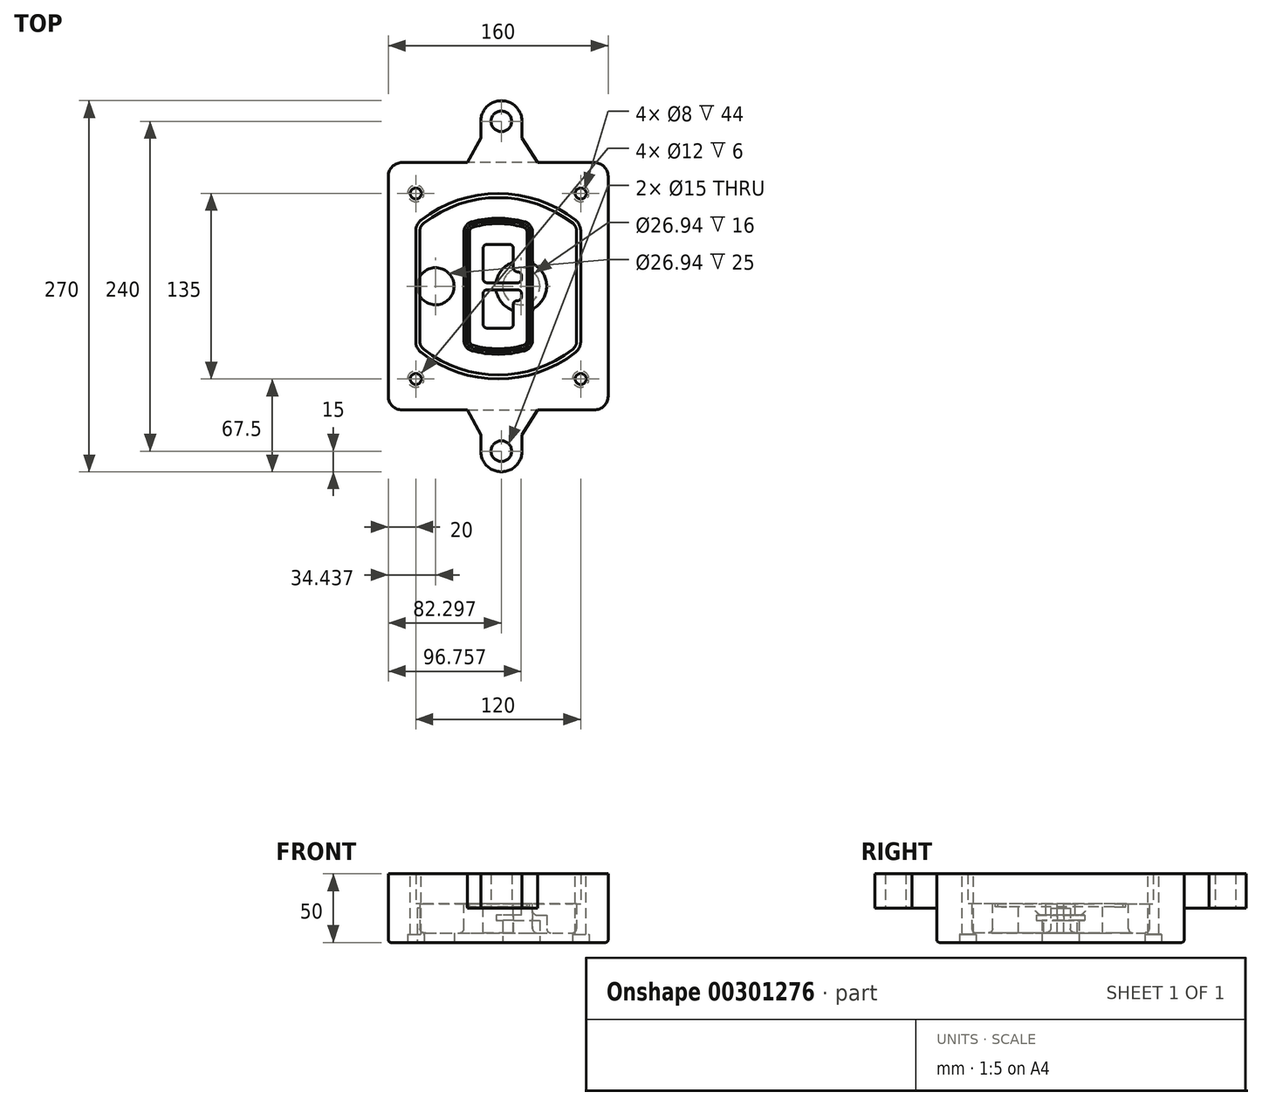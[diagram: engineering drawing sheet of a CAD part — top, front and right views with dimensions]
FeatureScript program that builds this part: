
annotation { "Feature Type Name" : "Feature", "Feature Type Description" : "" }
export const myFeature = defineFeature(function(context is Context, id is Id, definition is map)
    precondition{}
    {
        {
            var Q0;
            Q0=qCreatedBy(makeId("Top.planeOp"),FACE);
            var sketch = newSketch(context, id + "F0", { "sketchPlane" : qUnion([Q0])});
            skPoint(sketch, "E0.rect.middle", {"position": v(0, 0) * mm});
            skLineSegment(sketch, "E1.bottom", {"start": v(-70, -90) * mm, "end": v(70, -90) * mm});
            skLineSegment(sketch, "E1.top", {"start": v(-70, 90) * mm, "end": v(70, 90) * mm});
            skLineSegment(sketch, "E1.left", {"start": v(-80, -80) * mm, "end": v(-80, 80) * mm});
            skLineSegment(sketch, "E1.right", {"start": v(80, -80) * mm, "end": v(80, 80) * mm});
            skLineSegment(sketch, "E2", {"start": v(-80, 90) * mm, "end": v(80, -90) * mm, "construction": true});
            skLineSegment(sketch, "E3", {"start": v(80, 90) * mm, "end": v(-80, -90) * mm, "construction": true});
            skCircle(sketch, "E4", {"center": v(-60, 67.5) * mm, "radius": 4 * mm});
            skCircle(sketch, "E5", {"center": v(60, 67.5) * mm, "radius": 4 * mm});
            skCircle(sketch, "E6", {"center": v(60, -67.5) * mm, "radius": 4 * mm});
            skCircle(sketch, "E7", {"center": v(-60, -67.5) * mm, "radius": 4 * mm});
            skLineSegment(sketch, "E8", {"start": v(-60, 67.5) * mm, "end": v(60, 67.5) * mm, "construction": true});
            skLineSegment(sketch, "E9", {"start": v(60, 67.5) * mm, "end": v(60, -67.5) * mm, "construction": true});
            skLineSegment(sketch, "E10", {"start": v(60, -67.5) * mm, "end": v(-60, -67.5) * mm, "construction": true});
            skLineSegment(sketch, "E11", {"start": v(-60, -67.5) * mm, "end": v(-60, 67.5) * mm, "construction": true});
            skLineSegment(sketch, "E12", {"start": v(-60, 40.3) * mm, "end": v(-60, -40.3) * mm});
            skLineSegment(sketch, "E13", {"start": v(60, 40.3) * mm, "end": v(60, -40.3) * mm});
            skArc(sketch, "E14", {"start": v(56.15, 48.18) * mm, "mid": v(0, 67.5) * mm, "end": v(-56.15, 48.18) * mm});
            skArc(sketch, "E15", {"start": v(-56.15, -48.18) * mm, "mid": v(0, -67.5) * mm, "end": v(56.15, -48.18) * mm});
            skLineSegment(sketch, "E16", {"start": v(-60, 0) * mm, "end": v(60, 0) * mm, "construction": true});
            skPoint(sketch, "E17.visualSharp", {"position": v(-60, -45) * mm});
            skArc(sketch, "E17.filletArc", {"start": v(-60, -40.3) * mm, "mid": v(-58.99, -44.68) * mm, "end": v(-56.15, -48.18) * mm});
            skPoint(sketch, "E18.visualSharp", {"position": v(-60, 45) * mm});
            skArc(sketch, "E18.filletArc", {"start": v(-56.15, 48.18) * mm, "mid": v(-58.99, 44.68) * mm, "end": v(-60, 40.3) * mm});
            skPoint(sketch, "E19.visualSharp", {"position": v(60, 45) * mm});
            skArc(sketch, "E19.filletArc", {"start": v(60, 40.3) * mm, "mid": v(58.99, 44.68) * mm, "end": v(56.15, 48.18) * mm});
            skPoint(sketch, "E20.visualSharp", {"position": v(60, -45) * mm});
            skArc(sketch, "E20.filletArc", {"start": v(56.15, -48.18) * mm, "mid": v(58.99, -44.68) * mm, "end": v(60, -40.3) * mm});
            skPoint(sketch, "E21.visualSharp", {"position": v(-80, 90) * mm});
            skArc(sketch, "E21.filletArc", {"start": v(-70, 90) * mm, "mid": v(-77.07, 87.07) * mm, "end": v(-80, 80) * mm});
            skPoint(sketch, "E22.visualSharp", {"position": v(80, 90) * mm});
            skArc(sketch, "E22.filletArc", {"start": v(80, 80) * mm, "mid": v(77.07, 87.07) * mm, "end": v(70, 90) * mm});
            skPoint(sketch, "E23.visualSharp", {"position": v(80, -90) * mm});
            skArc(sketch, "E23.filletArc", {"start": v(70, -90) * mm, "mid": v(77.07, -87.07) * mm, "end": v(80, -80) * mm});
            skPoint(sketch, "E24.visualSharp", {"position": v(-80, -90) * mm});
            skArc(sketch, "E24.filletArc", {"start": v(-80, -80) * mm, "mid": v(-77.07, -87.07) * mm, "end": v(-70, -90) * mm});
            skArc(sketch, "E25.0", {"start": v(57, 40.3) * mm, "mid": v(56.3, 43.36) * mm, "end": v(54.3, 45.81) * mm});
            skLineSegment(sketch, "E25.1", {"start": v(57, 40.3) * mm, "end": v(57, -40.3) * mm});
            skArc(sketch, "E25.2", {"start": v(54.3, -45.81) * mm, "mid": v(56.3, -43.36) * mm, "end": v(57, -40.3) * mm});
            skArc(sketch, "E25.3", {"start": v(-54.3, -45.81) * mm, "mid": v(0, -64.5) * mm, "end": v(54.3, -45.81) * mm});
            skArc(sketch, "E25.4", {"start": v(-57, -40.3) * mm, "mid": v(-56.3, -43.36) * mm, "end": v(-54.3, -45.81) * mm});
            skArc(sketch, "E25.5", {"start": v(54.3, 45.81) * mm, "mid": v(0, 64.5) * mm, "end": v(-54.3, 45.81) * mm});
            skLineSegment(sketch, "E25.6", {"start": v(-57, 40.3) * mm, "end": v(-57, -40.3) * mm});
            skArc(sketch, "E25.7", {"start": v(-54.3, 45.81) * mm, "mid": v(-56.3, 43.36) * mm, "end": v(-57, 40.3) * mm});
            skArc(sketch, "E26.0", {"start": v(-58.62, 51.33) * mm, "mid": v(-62.58, 46.43) * mm, "end": v(-64, 40.3) * mm});
            skArc(sketch, "E26.1", {"start": v(58.62, 51.33) * mm, "mid": v(0, 71.5) * mm, "end": v(-58.62, 51.33) * mm});
            skArc(sketch, "E26.2", {"start": v(64, 40.3) * mm, "mid": v(62.58, 46.43) * mm, "end": v(58.62, 51.33) * mm});
            skLineSegment(sketch, "E26.3", {"start": v(64, 40.3) * mm, "end": v(64, -40.3) * mm});
            skArc(sketch, "E26.4", {"start": v(58.62, -51.33) * mm, "mid": v(62.58, -46.43) * mm, "end": v(64, -40.3) * mm});
            skLineSegment(sketch, "E26.5", {"start": v(-64, 40.3) * mm, "end": v(-64, -40.3) * mm});
            skArc(sketch, "E26.6", {"start": v(-58.62, -51.33) * mm, "mid": v(0, -71.5) * mm, "end": v(58.62, -51.33) * mm});
            skArc(sketch, "E26.7", {"start": v(-64, -40.3) * mm, "mid": v(-62.58, -46.43) * mm, "end": v(-58.62, -51.33) * mm});
            skSolve(sketch);
        }
        {
            var Q0;
            Q0=makeQuery(id+"F0.imprint","IMPRINT",FACE,{"disambiguationData":[TD([[makeQuery(id+"F0.imprint","IMPRINT",EDGE,{"derivedFrom":sQuery(id+"F0.wireOp",EDGE,"E1.bottom")}),1.0]])]});
            var Q1;
            Q1=makeQuery(id+"F0.imprint","IMPRINT",FACE,{"disambiguationData":[TD([[makeQuery(id+"F0.imprint","IMPRINT",EDGE,{"derivedFrom":sQuery(id+"F0.wireOp",EDGE,"E12")}),1.0]])]});
            var Q2;
            Q2=makeQuery(id+"F0.imprint","IMPRINT",FACE,{"disambiguationData":[TD([[makeQuery(id+"F0.imprint","IMPRINT",EDGE,{"derivedFrom":sQuery(id+"F0.wireOp",EDGE,"E25.0")}),1.0]])]});
            var Q3;
            Q3=makeQuery(id+"F0.imprint","IMPRINT",FACE,{"disambiguationData":[TD([[makeQuery(id+"F0.imprint","IMPRINT",EDGE,{"derivedFrom":sQuery(id+"F0.wireOp",EDGE,"E12")}),-1.0]])]});
            extrude(context, id + "F1", {"entities" : qUnion([Q0, Q1, Q2, Q3]), "oppositeDirection" : true, "depth" : 25 * mm});
        }
        {
            var Q0;
            Q0=makeQuery(id+"F0.imprint","IMPRINT",FACE,{"disambiguationData":[TD([[makeQuery(id+"F0.imprint","IMPRINT",EDGE,{"derivedFrom":sQuery(id+"F0.wireOp",EDGE,"E12")}),1.0]])]});
            extrude(context, id + "F2", {"entities" : qUnion([Q0]), "operationType" : NewBodyOperationType.ADD, "depth" : 3 * mm});
        }
        {
            var Q0;
            Q0=makeQuery(id+"F0.imprint","IMPRINT",FACE,{"disambiguationData":[TD([[makeQuery(id+"F0.imprint","IMPRINT",EDGE,{"derivedFrom":sQuery(id+"F0.wireOp",EDGE,"E25.0")}),1.0]])]});
            extrude(context, id + "F3", {"entities" : qUnion([Q0]), "operationType" : NewBodyOperationType.REMOVE, "oppositeDirection" : true, "depth" : 18 * mm});
        }
        {
            var Q0;
            Q0=makeQuery(id+"F2.opExtrude","CAP_FACE",FACE,{"disambiguationData":[OSD([sQuery(id+"F0.wireOp",EDGE,"E12"),sQuery(id+"F0.wireOp",EDGE,"E13"),sQuery(id+"F0.wireOp",EDGE,"E14"),sQuery(id+"F0.wireOp",EDGE,"E15"),sQuery(id+"F0.wireOp",EDGE,"E17.filletArc"),sQuery(id+"F0.wireOp",EDGE,"E18.filletArc"),sQuery(id+"F0.wireOp",EDGE,"E19.filletArc"),sQuery(id+"F0.wireOp",EDGE,"E20.filletArc"),sQuery(id+"F0.wireOp",EDGE,"E25.0"),sQuery(id+"F0.wireOp",EDGE,"E25.1"),sQuery(id+"F0.wireOp",EDGE,"E25.2"),sQuery(id+"F0.wireOp",EDGE,"E25.3"),sQuery(id+"F0.wireOp",EDGE,"E25.4"),sQuery(id+"F0.wireOp",EDGE,"E25.5"),sQuery(id+"F0.wireOp",EDGE,"E25.6"),sQuery(id+"F0.wireOp",EDGE,"E25.7")])],"isStart":false});
            var sketch = newSketch(context, id + "F4", { "sketchPlane" : qUnion([Q0])});
            skArc(sketch, "E27.0", {"start": v(-19.08, -46.97) * mm, "mid": v(0, -49.5) * mm, "end": v(19.08, -46.97) * mm});
            skArc(sketch, "E28.0", {"start": v(19.08, 46.97) * mm, "mid": v(0, 49.5) * mm, "end": v(-19.08, 46.97) * mm});
            skLineSegment(sketch, "E29", {"start": v(-25, 39.25) * mm, "end": v(-25, -39.25) * mm});
            skLineSegment(sketch, "E30", {"start": v(25, 39.25) * mm, "end": v(25, -39.25) * mm});
            skLineSegment(sketch, "E31", {"start": v(-25, 45.1) * mm, "end": v(25, 45.1) * mm, "construction": true});
            skLineSegment(sketch, "E32", {"start": v(-25, -45.1) * mm, "end": v(25, -45.1) * mm, "construction": true});
            skPoint(sketch, "E33.visualSharp", {"position": v(-25, 45.1) * mm});
            skArc(sketch, "E33.filletArc", {"start": v(-19.08, 46.97) * mm, "mid": v(-23.35, 44.11) * mm, "end": v(-25, 39.25) * mm});
            skPoint(sketch, "E34.visualSharp", {"position": v(25, 45.1) * mm});
            skArc(sketch, "E34.filletArc", {"start": v(25, 39.25) * mm, "mid": v(23.35, 44.11) * mm, "end": v(19.08, 46.97) * mm});
            skPoint(sketch, "E35.visualSharp", {"position": v(25, -45.1) * mm});
            skArc(sketch, "E35.filletArc", {"start": v(19.08, -46.97) * mm, "mid": v(23.35, -44.11) * mm, "end": v(25, -39.25) * mm});
            skPoint(sketch, "E36.visualSharp", {"position": v(-25, -45.1) * mm});
            skArc(sketch, "E36.filletArc", {"start": v(-25, -39.25) * mm, "mid": v(-23.35, -44.11) * mm, "end": v(-19.08, -46.97) * mm});
            skArc(sketch, "E37.0", {"start": v(54.3, 45.81) * mm, "mid": v(0, 64.5) * mm, "end": v(-54.3, 45.81) * mm});
            skArc(sketch, "E37.1", {"start": v(-54.3, 45.81) * mm, "mid": v(-56.3, 43.36) * mm, "end": v(-57, 40.3) * mm});
            skLineSegment(sketch, "E37.2", {"start": v(-57, 40.3) * mm, "end": v(-57, -40.3) * mm});
            skArc(sketch, "E37.3", {"start": v(-57, -40.3) * mm, "mid": v(-56.3, -43.36) * mm, "end": v(-54.3, -45.81) * mm});
            skArc(sketch, "E37.4", {"start": v(-54.3, -45.81) * mm, "mid": v(0, -64.5) * mm, "end": v(54.3, -45.81) * mm});
            skArc(sketch, "E37.5", {"start": v(54.3, -45.81) * mm, "mid": v(56.3, -43.36) * mm, "end": v(57, -40.3) * mm});
            skLineSegment(sketch, "E37.6", {"start": v(57, 40.3) * mm, "end": v(57, -40.3) * mm});
            skArc(sketch, "E37.7", {"start": v(57, 40.3) * mm, "mid": v(56.3, 43.36) * mm, "end": v(54.3, 45.81) * mm});
            skLineSegment(sketch, "E38.0", {"start": v(23, 39.25) * mm, "end": v(23, -39.25) * mm});
            skArc(sketch, "E38.1", {"start": v(18.56, -45.04) * mm, "mid": v(21.76, -42.9) * mm, "end": v(23, -39.25) * mm});
            skArc(sketch, "E38.2", {"start": v(-18.56, -45.04) * mm, "mid": v(0, -47.5) * mm, "end": v(18.56, -45.04) * mm});
            skArc(sketch, "E38.3", {"start": v(-23, -39.25) * mm, "mid": v(-21.76, -42.9) * mm, "end": v(-18.56, -45.04) * mm});
            skLineSegment(sketch, "E38.4", {"start": v(-23, 39.25) * mm, "end": v(-23, -39.25) * mm});
            skArc(sketch, "E38.5", {"start": v(23, 39.25) * mm, "mid": v(21.76, 42.9) * mm, "end": v(18.56, 45.04) * mm});
            skArc(sketch, "E38.6", {"start": v(-18.56, 45.04) * mm, "mid": v(-21.76, 42.9) * mm, "end": v(-23, 39.25) * mm});
            skArc(sketch, "E38.7", {"start": v(18.56, 45.04) * mm, "mid": v(0, 47.5) * mm, "end": v(-18.56, 45.04) * mm});
            skArc(sketch, "E39.0", {"start": v(21, 39.25) * mm, "mid": v(20.18, 41.68) * mm, "end": v(18.04, 43.1) * mm});
            skLineSegment(sketch, "E39.1", {"start": v(21, 39.25) * mm, "end": v(21, -39.25) * mm});
            skArc(sketch, "E39.2", {"start": v(18.04, -43.1) * mm, "mid": v(20.18, -41.68) * mm, "end": v(21, -39.25) * mm});
            skArc(sketch, "E39.3", {"start": v(-18.04, -43.1) * mm, "mid": v(0, -45.5) * mm, "end": v(18.04, -43.1) * mm});
            skArc(sketch, "E39.4", {"start": v(-21, -39.25) * mm, "mid": v(-20.18, -41.68) * mm, "end": v(-18.04, -43.1) * mm});
            skArc(sketch, "E39.5", {"start": v(18.04, 43.1) * mm, "mid": v(0, 45.5) * mm, "end": v(-18.04, 43.1) * mm});
            skLineSegment(sketch, "E39.6", {"start": v(-21, 39.25) * mm, "end": v(-21, -39.25) * mm});
            skArc(sketch, "E39.7", {"start": v(-18.04, 43.1) * mm, "mid": v(-20.18, 41.68) * mm, "end": v(-21, 39.25) * mm});
            skLineSegment(sketch, "E40", {"start": v(-25, 0) * mm, "end": v(25, 0) * mm, "construction": true});
            skLineSegment(sketch, "E41", {"start": v(-11, 5.5) * mm, "end": v(-11, 27.5) * mm});
            skLineSegment(sketch, "E42", {"start": v(-8, 30.5) * mm, "end": v(8, 30.5) * mm});
            skLineSegment(sketch, "E43", {"start": v(11, 27.5) * mm, "end": v(11, 13.5) * mm});
            skLineSegment(sketch, "E44", {"start": v(14, 10.5) * mm, "end": v(14, 10.5) * mm});
            skLineSegment(sketch, "E45", {"start": v(17, 7.5) * mm, "end": v(17, 5.5) * mm});
            skLineSegment(sketch, "E46", {"start": v(14, 2.5) * mm, "end": v(-8, 2.5) * mm});
            skPoint(sketch, "E47.visualSharp", {"position": v(-11, 30.5) * mm});
            skArc(sketch, "E47.filletArc", {"start": v(-8, 30.5) * mm, "mid": v(-10.12, 29.62) * mm, "end": v(-11, 27.5) * mm});
            skPoint(sketch, "E48.visualSharp", {"position": v(11, 30.5) * mm});
            skArc(sketch, "E48.filletArc", {"start": v(11, 27.5) * mm, "mid": v(10.12, 29.62) * mm, "end": v(8, 30.5) * mm});
            skPoint(sketch, "E49.visualSharp", {"position": v(11, 10.5) * mm});
            skArc(sketch, "E49.filletArc", {"start": v(11, 13.5) * mm, "mid": v(11.88, 11.38) * mm, "end": v(14, 10.5) * mm});
            skPoint(sketch, "E50.visualSharp", {"position": v(17, 10.5) * mm});
            skArc(sketch, "E50.filletArc", {"start": v(17, 7.5) * mm, "mid": v(16.12, 9.62) * mm, "end": v(14, 10.5) * mm});
            skPoint(sketch, "E51.visualSharp", {"position": v(17, 2.5) * mm});
            skArc(sketch, "E51.filletArc", {"start": v(14, 2.5) * mm, "mid": v(16.12, 3.38) * mm, "end": v(17, 5.5) * mm});
            skPoint(sketch, "E52.visualSharp", {"position": v(-11, 2.5) * mm});
            skArc(sketch, "E52.filletArc", {"start": v(-11, 5.5) * mm, "mid": v(-10.12, 3.38) * mm, "end": v(-8, 2.5) * mm});
            skLineSegment(sketch, "E53.0.MirrorCS", {"start": v(14, -2.5) * mm, "end": v(-8, -2.5) * mm});
            skArc(sketch, "E54.0.MirrorCS", {"start": v(-11, -5.5) * mm, "mid": v(-10.12, -3.38) * mm, "end": v(-8, -2.5) * mm});
            skLineSegment(sketch, "E55.0.MirrorCS", {"start": v(-11, -5.5) * mm, "end": v(-11, -27.5) * mm});
            skArc(sketch, "E56.0.MirrorCS", {"start": v(-8, -30.5) * mm, "mid": v(-10.12, -29.62) * mm, "end": v(-11, -27.5) * mm});
            skLineSegment(sketch, "E57.0.MirrorCS", {"start": v(-8, -30.5) * mm, "end": v(8, -30.5) * mm});
            skArc(sketch, "E58.0.MirrorCS", {"start": v(11, -27.5) * mm, "mid": v(10.12, -29.62) * mm, "end": v(8, -30.5) * mm});
            skLineSegment(sketch, "E59.0.MirrorCS", {"start": v(11, -27.5) * mm, "end": v(11, -13.5) * mm});
            skArc(sketch, "E60.0.MirrorCS", {"start": v(11, -13.5) * mm, "mid": v(11.88, -11.38) * mm, "end": v(14, -10.5) * mm});
            skArc(sketch, "E61.0.MirrorCS", {"start": v(17, -7.5) * mm, "mid": v(16.12, -9.62) * mm, "end": v(14, -10.5) * mm});
            skLineSegment(sketch, "E62.0.MirrorCS", {"start": v(17, -7.5) * mm, "end": v(17, -5.5) * mm});
            skArc(sketch, "E63.0.MirrorCS", {"start": v(14, -2.5) * mm, "mid": v(16.12, -3.38) * mm, "end": v(17, -5.5) * mm});
            skSolve(sketch);
        }
        {
            var Q0;
            Q0=makeQuery(id+"F4.imprint","IMPRINT",FACE,{"disambiguationData":[TD([[makeQuery(id+"F4.imprint","IMPRINT",EDGE,{"derivedFrom":sQuery(id+"F4.wireOp",EDGE,"E27.0")}),1.0]])]});
            var Q1;
            Q1=makeQuery(id+"F4.imprint","IMPRINT",FACE,{"disambiguationData":[TD([[makeQuery(id+"F4.imprint","IMPRINT",EDGE,{"derivedFrom":sQuery(id+"F4.wireOp",EDGE,"E38.0")}),-1.0]])]});
            var Q2;
            Q2=makeQuery(id+"F4.imprint","IMPRINT",FACE,{"disambiguationData":[TD([[makeQuery(id+"F4.imprint","IMPRINT",EDGE,{"derivedFrom":sQuery(id+"F4.wireOp",EDGE,"E39.0")}),1.0]])]});
            extrude(context, id + "F5", {"entities" : qUnion([Q0, Q1, Q2]), "operationType" : NewBodyOperationType.ADD, "endBound" : BoundingType.UP_TO_NEXT, "oppositeDirection" : true, "depth" : 25 * mm});
        }
        {
            var Q0;
            Q0=makeQuery(id+"F4.imprint","IMPRINT",FACE,{"disambiguationData":[TD([[makeQuery(id+"F4.imprint","IMPRINT",EDGE,{"derivedFrom":sQuery(id+"F4.wireOp",EDGE,"E38.0")}),-1.0]])]});
            extrude(context, id + "F6", {"entities" : qUnion([Q0]), "operationType" : NewBodyOperationType.REMOVE, "oppositeDirection" : true, "depth" : 2 * mm});
        }
        {
            var Q0;
            Q0=makeQuery(id+"F1.opExtrude","CAP_FACE",FACE,{"disambiguationData":[OSD([sQuery(id+"F0.wireOp",EDGE,"E1.bottom"),sQuery(id+"F0.wireOp",EDGE,"E1.top"),sQuery(id+"F0.wireOp",EDGE,"E1.left"),sQuery(id+"F0.wireOp",EDGE,"E1.right"),sQuery(id+"F0.wireOp",EDGE,"E4"),sQuery(id+"F0.wireOp",EDGE,"E5"),sQuery(id+"F0.wireOp",EDGE,"E6"),sQuery(id+"F0.wireOp",EDGE,"E7"),sQuery(id+"F0.wireOp",EDGE,"E21.filletArc"),sQuery(id+"F0.wireOp",EDGE,"E22.filletArc"),sQuery(id+"F0.wireOp",EDGE,"E23.filletArc"),sQuery(id+"F0.wireOp",EDGE,"E24.filletArc")])],"isStart":false});
            var sketch = newSketch(context, id + "F7", { "sketchPlane" : qUnion([Q0])});
            skCircle(sketch, "E64", {"center": v(16.76, 0) * mm, "radius": 13.47 * mm});
            skCircle(sketch, "E65", {"center": v(-45.56, 0) * mm, "radius": 13.47 * mm});
            skLineSegment(sketch, "E66", {"start": v(80, 0) * mm, "end": v(-80, 0) * mm});
            skCircle(sketch, "E67", {"center": v(16.76, 0) * mm, "radius": 18.47 * mm});
            skCircle(sketch, "E68", {"center": v(60, -67.5) * mm, "radius": 6 * mm});
            skCircle(sketch, "E69", {"center": v(-60, -67.5) * mm, "radius": 6 * mm});
            skCircle(sketch, "E70", {"center": v(-60, 67.5) * mm, "radius": 6 * mm});
            skCircle(sketch, "E71", {"center": v(60, 67.5) * mm, "radius": 6 * mm});
            skSolve(sketch);
        }
        {
            var Q0;
            {var subQ1=sQuery(id+"F7.wireOp",EDGE,"E66");var subQ4=sQuery(id+"F7.wireOp",EDGE,"E64");var subQ6=makeQuery(id+"F7.imprint","INTERSECT",VERTEX,{"disambiguationData":[OD(0.0)],"derivedFrom":[subQ4,subQ1]});Q0=makeQuery(id+"F7.imprint","IMPRINT",FACE,{"disambiguationData":[TD([[makeQuery(id+"F7.imprint","IMPRINT",EDGE,{"disambiguationData":[TD([[subQ6,-1.0]])],"derivedFrom":subQ4}),-1.0]])]});}
            var Q1;
            {var subQ0=sQuery(id+"F7.wireOp",EDGE,"E66");var subQ1=sQuery(id+"F7.wireOp",EDGE,"E64");var subQ3=makeQuery(id+"F7.imprint","INTERSECT",VERTEX,{"disambiguationData":[OD(0.0)],"derivedFrom":[subQ1,subQ0]});Q1=makeQuery(id+"F7.imprint","IMPRINT",FACE,{"disambiguationData":[TD([[makeQuery(id+"F7.imprint","IMPRINT",EDGE,{"disambiguationData":[TD([[subQ3,-1.0]])],"derivedFrom":subQ1}),1.0]])]});}
            var Q2;
            {var subQ0=sQuery(id+"F7.wireOp",EDGE,"E66");var subQ1=sQuery(id+"F7.wireOp",EDGE,"E64");var subQ3=makeQuery(id+"F7.imprint","INTERSECT",VERTEX,{"disambiguationData":[OD(0.0)],"derivedFrom":[subQ1,subQ0]});Q2=makeQuery(id+"F7.imprint","IMPRINT",FACE,{"disambiguationData":[TD([[makeQuery(id+"F7.imprint","IMPRINT",EDGE,{"disambiguationData":[TD([[subQ3,1.0]])],"derivedFrom":subQ1}),1.0]])]});}
            var Q3;
            {var subQ1=sQuery(id+"F7.wireOp",EDGE,"E66");var subQ4=sQuery(id+"F7.wireOp",EDGE,"E64");var subQ6=makeQuery(id+"F7.imprint","INTERSECT",VERTEX,{"disambiguationData":[OD(0.0)],"derivedFrom":[subQ4,subQ1]});Q3=makeQuery(id+"F7.imprint","IMPRINT",FACE,{"disambiguationData":[TD([[makeQuery(id+"F7.imprint","IMPRINT",EDGE,{"disambiguationData":[TD([[subQ6,1.0]])],"derivedFrom":subQ4}),-1.0]])]});}
            extrude(context, id + "F8", {"entities" : qUnion([Q0, Q1, Q2, Q3]), "operationType" : NewBodyOperationType.ADD, "oppositeDirection" : true, "depth" : 20 * mm});
        }
        {
            var Q0;
            {var subQ0=sQuery(id+"F7.wireOp",EDGE,"E66");var subQ1=sQuery(id+"F7.wireOp",EDGE,"E64");var subQ3=makeQuery(id+"F7.imprint","INTERSECT",VERTEX,{"disambiguationData":[OD(0.0)],"derivedFrom":[subQ1,subQ0]});Q0=makeQuery(id+"F7.imprint","IMPRINT",FACE,{"disambiguationData":[TD([[makeQuery(id+"F7.imprint","IMPRINT",EDGE,{"disambiguationData":[TD([[subQ3,-1.0]])],"derivedFrom":subQ1}),1.0]])]});}
            var Q1;
            {var subQ0=sQuery(id+"F7.wireOp",EDGE,"E66");var subQ1=sQuery(id+"F7.wireOp",EDGE,"E64");var subQ3=makeQuery(id+"F7.imprint","INTERSECT",VERTEX,{"disambiguationData":[OD(0.0)],"derivedFrom":[subQ1,subQ0]});Q1=makeQuery(id+"F7.imprint","IMPRINT",FACE,{"disambiguationData":[TD([[makeQuery(id+"F7.imprint","IMPRINT",EDGE,{"disambiguationData":[TD([[subQ3,1.0]])],"derivedFrom":subQ1}),1.0]])]});}
            extrude(context, id + "F9", {"entities" : qUnion([Q0, Q1]), "operationType" : NewBodyOperationType.REMOVE, "oppositeDirection" : true, "depth" : 16 * mm});
        }
        {
            var Q0;
            {var subQ0=sQuery(id+"F7.wireOp",EDGE,"E66");var subQ1=sQuery(id+"F7.wireOp",EDGE,"E65");var subQ3=makeQuery(id+"F7.imprint","INTERSECT",VERTEX,{"disambiguationData":[OD(0.0)],"derivedFrom":[subQ1,subQ0]});Q0=makeQuery(id+"F7.imprint","IMPRINT",FACE,{"disambiguationData":[TD([[makeQuery(id+"F7.imprint","IMPRINT",EDGE,{"disambiguationData":[TD([[subQ3,-1.0]])],"derivedFrom":subQ1}),1.0]])]});}
            var Q1;
            {var subQ0=sQuery(id+"F7.wireOp",EDGE,"E66");var subQ1=sQuery(id+"F7.wireOp",EDGE,"E65");var subQ3=makeQuery(id+"F7.imprint","INTERSECT",VERTEX,{"disambiguationData":[OD(0.0)],"derivedFrom":[subQ1,subQ0]});Q1=makeQuery(id+"F7.imprint","IMPRINT",FACE,{"disambiguationData":[TD([[makeQuery(id+"F7.imprint","IMPRINT",EDGE,{"disambiguationData":[TD([[subQ3,1.0]])],"derivedFrom":subQ1}),1.0]])]});}
            extrude(context, id + "F10", {"entities" : qUnion([Q0, Q1]), "operationType" : NewBodyOperationType.REMOVE, "oppositeDirection" : true, "depth" : 25 * mm});
        }
        {
            var Q0;
            Q0=makeQuery(id+"F7.imprint","IMPRINT",FACE,{"disambiguationData":[TD([[makeQuery(id+"F7.imprint","IMPRINT",EDGE,{"derivedFrom":sQuery(id+"F7.wireOp",EDGE,"E68")}),1.0]])]});
            var Q1;
            Q1=makeQuery(id+"F7.imprint","IMPRINT",FACE,{"disambiguationData":[TD([[makeQuery(id+"F7.imprint","IMPRINT",EDGE,{"derivedFrom":makeQuery(id+"F1.opExtrude","CAP_EDGE",EDGE,{"disambiguationData":[OSD([sQuery(id+"F0.wireOp",EDGE,"E5")])],"isStart":false})}),-1.0]])]});
            var Q2;
            Q2=makeQuery(id+"F7.imprint","IMPRINT",FACE,{"disambiguationData":[TD([[makeQuery(id+"F7.imprint","IMPRINT",EDGE,{"derivedFrom":sQuery(id+"F7.wireOp",EDGE,"E69")}),1.0]])]});
            var Q3;
            Q3=makeQuery(id+"F7.imprint","IMPRINT",FACE,{"disambiguationData":[TD([[makeQuery(id+"F7.imprint","IMPRINT",EDGE,{"derivedFrom":makeQuery(id+"F1.opExtrude","CAP_EDGE",EDGE,{"disambiguationData":[OSD([sQuery(id+"F0.wireOp",EDGE,"E4")])],"isStart":false})}),-1.0]])]});
            var Q4;
            Q4=makeQuery(id+"F7.imprint","IMPRINT",FACE,{"disambiguationData":[TD([[makeQuery(id+"F7.imprint","IMPRINT",EDGE,{"derivedFrom":sQuery(id+"F7.wireOp",EDGE,"E70")}),1.0]])]});
            var Q5;
            Q5=makeQuery(id+"F7.imprint","IMPRINT",FACE,{"disambiguationData":[TD([[makeQuery(id+"F7.imprint","IMPRINT",EDGE,{"derivedFrom":makeQuery(id+"F1.opExtrude","CAP_EDGE",EDGE,{"disambiguationData":[OSD([sQuery(id+"F0.wireOp",EDGE,"E7")])],"isStart":false})}),-1.0]])]});
            var Q6;
            Q6=makeQuery(id+"F7.imprint","IMPRINT",FACE,{"disambiguationData":[TD([[makeQuery(id+"F7.imprint","IMPRINT",EDGE,{"derivedFrom":sQuery(id+"F7.wireOp",EDGE,"E71")}),1.0]])]});
            var Q7;
            Q7=makeQuery(id+"F7.imprint","IMPRINT",FACE,{"disambiguationData":[TD([[makeQuery(id+"F7.imprint","IMPRINT",EDGE,{"derivedFrom":makeQuery(id+"F1.opExtrude","CAP_EDGE",EDGE,{"disambiguationData":[OSD([sQuery(id+"F0.wireOp",EDGE,"E6")])],"isStart":false})}),-1.0]])]});
            extrude(context, id + "F11", {"entities" : qUnion([Q0, Q1, Q2, Q3, Q4, Q5, Q6, Q7]), "operationType" : NewBodyOperationType.REMOVE, "oppositeDirection" : true, "depth" : 6 * mm});
        }
        {
            var Q0;
            Q0=makeQuery(id+"F9.boolean.opBoolean","COPY",FACE,{"derivedFrom":makeQuery(id+"F9.opExtrude","CAP_FACE",FACE,{"disambiguationData":[OSD([sQuery(id+"F7.wireOp",EDGE,"E64")])],"isStart":false})});
            var sketch = newSketch(context, id + "F12", { "sketchPlane" : qUnion([Q0])});
            skArc(sketch, "E72.0", {"start": v(11, 17.55) * mm, "mid": v(2.57, 11.82) * mm, "end": v(-1.54, 2.5) * mm});
            skArc(sketch, "E72.1", {"start": v(-1.54, -2.5) * mm, "mid": v(2.57, -11.82) * mm, "end": v(11, -17.55) * mm});
            skLineSegment(sketch, "E73", {"start": v(-1.54, -2.5) * mm, "end": v(14, -2.5) * mm});
            skLineSegment(sketch, "E74.0", {"start": v(14, 2.5) * mm, "end": v(-1.54, 2.5) * mm});
            skArc(sketch, "E74.1", {"start": v(14, 2.5) * mm, "mid": v(16.12, 3.38) * mm, "end": v(17, 5.5) * mm});
            skLineSegment(sketch, "E74.2", {"start": v(17, 7.5) * mm, "end": v(17, 5.5) * mm});
            skArc(sketch, "E74.3", {"start": v(17, 7.5) * mm, "mid": v(16.12, 9.62) * mm, "end": v(14, 10.5) * mm});
            skArc(sketch, "E74.4", {"start": v(11, 13.5) * mm, "mid": v(11.88, 11.38) * mm, "end": v(14, 10.5) * mm});
            skLineSegment(sketch, "E74.5", {"start": v(11, 17.55) * mm, "end": v(11, 13.5) * mm});
            skLineSegment(sketch, "E74.7", {"start": v(14, -2.5) * mm, "end": v(-1.54, -2.5) * mm});
            skArc(sketch, "E74.8", {"start": v(14, -2.5) * mm, "mid": v(16.12, -3.38) * mm, "end": v(17, -5.5) * mm});
            skLineSegment(sketch, "E74.9", {"start": v(17, -7.5) * mm, "end": v(17, -5.5) * mm});
            skArc(sketch, "E74.10", {"start": v(17, -7.5) * mm, "mid": v(16.12, -9.62) * mm, "end": v(14, -10.5) * mm});
            skArc(sketch, "E74.11", {"start": v(11, -13.5) * mm, "mid": v(11.88, -11.38) * mm, "end": v(14, -10.5) * mm});
            skLineSegment(sketch, "E74.12", {"start": v(11, -17.55) * mm, "end": v(11, -13.5) * mm});
            skPoint(sketch, "E75.orphan", {"position": v(11, -27.5) * mm});
            skPoint(sketch, "E76.orphan", {"position": v(-8, -2.5) * mm});
            skPoint(sketch, "E77.orphan", {"position": v(-8, 2.5) * mm});
            skPoint(sketch, "E78.orphan", {"position": v(11, 27.5) * mm});
            skSolve(sketch);
        }
        {
            var Q0;
            {var subQ7=sQuery(id+"F12.wireOp",EDGE,"E72.0");var subQ14=sQuery(id+"F12.wireOp",EDGE,"E72.1");var subQ16=sQuery(id+"F12.wireOp",EDGE,"E74.1");var subQ18=sQuery(id+"F12.wireOp",EDGE,"E74.8");Q0=qUnion([makeQuery(id+"F12.imprint","IMPRINT",FACE,{"disambiguationData":[TD([[makeQuery(id+"F12.imprint","IMPRINT",EDGE,{"derivedFrom":subQ7}),1.0]])]}),makeQuery(id+"F12.imprint","IMPRINT",FACE,{"disambiguationData":[TD([[makeQuery(id+"F12.imprint","IMPRINT",EDGE,{"derivedFrom":subQ14}),1.0]])]}),makeQuery(id+"F12.imprint","IMPRINT",FACE,{"disambiguationData":[TD([[makeQuery(id+"F12.imprint","IMPRINT",EDGE,{"derivedFrom":subQ16}),1.0]])]}),makeQuery(id+"F12.imprint","IMPRINT",FACE,{"disambiguationData":[TD([[makeQuery(id+"F12.imprint","IMPRINT",EDGE,{"derivedFrom":subQ18}),-1.0]])]})]);}
            var Q1;
            Q1=makeQuery(id+"F5.boolean.opBoolean","SPLIT",FACE,{"disambiguationData":[TD([makeQuery(id+"F5.opExtrude","SWEPT_FACE",FACE,{"disambiguationData":[OSD([sQuery(id+"F4.wireOp",EDGE,"E41")])]})])],"derivedFrom":makeQuery(id+"F3.boolean.opBoolean","COPY",FACE,{"derivedFrom":makeQuery(id+"F3.opExtrude","CAP_FACE",FACE,{"disambiguationData":[OSD([sQuery(id+"F0.wireOp",EDGE,"E25.0"),sQuery(id+"F0.wireOp",EDGE,"E25.1"),sQuery(id+"F0.wireOp",EDGE,"E25.2"),sQuery(id+"F0.wireOp",EDGE,"E25.3"),sQuery(id+"F0.wireOp",EDGE,"E25.4"),sQuery(id+"F0.wireOp",EDGE,"E25.5"),sQuery(id+"F0.wireOp",EDGE,"E25.6"),sQuery(id+"F0.wireOp",EDGE,"E25.7")])],"isStart":false})})});
            extrude(context, id + "F13", {"entities" : qUnion([Q0]), "operationType" : NewBodyOperationType.REMOVE, "endBound" : BoundingType.UP_TO_SURFACE, "endBoundEntityFace" : qUnion([Q1]), "depth" : 25 * mm});
        }
        {
            var Q0;
            Q0=makeQuery(id+"F3.boolean.opBoolean","COPY",EDGE,{"derivedFrom":makeQuery(id+"F3.opExtrude","CAP_EDGE",EDGE,{"disambiguationData":[OSD([sQuery(id+"F0.wireOp",EDGE,"E25.6")])],"isStart":false})});
            var Q1;
            Q1=makeQuery(id+"F8.boolean.opBoolean","INTERSECT",EDGE,{"derivedFrom":[makeQuery(id+"F5.opExtrude","SWEPT_FACE",FACE,{"disambiguationData":[OSD([sQuery(id+"F4.wireOp",EDGE,"E30")])]}),makeQuery(id+"F8.opExtrude","CAP_FACE",FACE,{"disambiguationData":[OSD([sQuery(id+"F7.wireOp",EDGE,"E67")])],"isStart":false})]});
            var Q2;
            Q2=makeQuery(id+"F8.boolean.opBoolean","INTERSECT",EDGE,{"disambiguationData":[OD(1.0)],"derivedFrom":[makeQuery(id+"F5.opExtrude","SWEPT_FACE",FACE,{"disambiguationData":[OSD([sQuery(id+"F4.wireOp",EDGE,"E30")])]}),makeQuery(id+"F8.opExtrude","SWEPT_FACE",FACE,{"disambiguationData":[OSD([sQuery(id+"F7.wireOp",EDGE,"E67")])]})]});
            var Q3;
            {var subQ0=sQuery(id+"F4.wireOp",EDGE,"E30");Q3=makeQuery(id+"F8.boolean.opBoolean","SPLIT",EDGE,{"disambiguationData":[TD([makeQuery(id+"F5.opExtrude","SWEPT_FACE",FACE,{"disambiguationData":[OSD([sQuery(id+"F4.wireOp",EDGE,"E35.filletArc")])]})])],"derivedFrom":makeQuery(id+"F5.opExtrude","CAP_EDGE",EDGE,{"disambiguationData":[OSD([subQ0])],"isStart":false})});}
            var Q4;
            {var subQ0=sQuery(id+"F0.wireOp",EDGE,"E25.7");var subQ1=sQuery(id+"F0.wireOp",EDGE,"E25.1");var subQ2=sQuery(id+"F0.wireOp",EDGE,"E25.6");var subQ3=sQuery(id+"F0.wireOp",EDGE,"E25.5");var subQ4=sQuery(id+"F0.wireOp",EDGE,"E25.4");var subQ5=sQuery(id+"F0.wireOp",EDGE,"E25.0");var subQ6=sQuery(id+"F0.wireOp",EDGE,"E25.2");var subQ7=sQuery(id+"F0.wireOp",EDGE,"E25.3");Q4=makeQuery(id+"F8.boolean.opBoolean","INTERSECT",EDGE,{"derivedFrom":[makeQuery(id+"F5.boolean.opBoolean","SPLIT",FACE,{"disambiguationData":[TD([makeQuery(id+"F2.opExtrude","SWEPT_FACE",FACE,{"disambiguationData":[OSD([subQ5])]})])],"derivedFrom":makeQuery(id+"F3.boolean.opBoolean","COPY",FACE,{"derivedFrom":makeQuery(id+"F3.opExtrude","CAP_FACE",FACE,{"disambiguationData":[OSD([subQ5,subQ1,subQ6,subQ7,subQ4,subQ3,subQ2,subQ0])],"isStart":false})})}),makeQuery(id+"F8.opExtrude","SWEPT_FACE",FACE,{"disambiguationData":[OSD([sQuery(id+"F7.wireOp",EDGE,"E67")])]})]});}
            var Q5;
            Q5=makeQuery(id+"F8.boolean.opBoolean","INTERSECT",EDGE,{"disambiguationData":[OD(0.0)],"derivedFrom":[makeQuery(id+"F5.opExtrude","SWEPT_FACE",FACE,{"disambiguationData":[OSD([sQuery(id+"F4.wireOp",EDGE,"E30")])]}),makeQuery(id+"F8.opExtrude","SWEPT_FACE",FACE,{"disambiguationData":[OSD([sQuery(id+"F7.wireOp",EDGE,"E67")])]})]});
            fillet(context, id + "F14", {"entities" : qUnion([Q0, Q1, Q2, Q3, Q4, Q5]), "radius" : 3 * mm, "tangentPropagation" : true, "allowEdgeOverflow" : false});
        }
        {
            var Q0;
            Q0=makeQuery(id+"F1.opExtrude","CAP_EDGE",EDGE,{"disambiguationData":[OSD([sQuery(id+"F0.wireOp",EDGE,"E1.bottom")])],"isStart":false});
            fillet(context, id + "F15", {"entities" : qUnion([Q0]), "radius" : 2 * mm, "tangentPropagation" : true, "allowEdgeOverflow" : false});
        }
        {
            var Q0;
            {var subQ0=sQuery(id+"F0.wireOp",EDGE,"E21.filletArc");var subQ1=sQuery(id+"F0.wireOp",EDGE,"E7");var subQ2=sQuery(id+"F0.wireOp",EDGE,"E6");var subQ3=sQuery(id+"F0.wireOp",EDGE,"E5");var subQ4=sQuery(id+"F0.wireOp",EDGE,"E4");var subQ5=sQuery(id+"F0.wireOp",EDGE,"E22.filletArc");var subQ6=sQuery(id+"F0.wireOp",EDGE,"E1.bottom");var subQ7=sQuery(id+"F0.wireOp",EDGE,"E1.right");var subQ8=sQuery(id+"F0.wireOp",EDGE,"E1.top");var subQ9=sQuery(id+"F0.wireOp",EDGE,"E1.left");var subQ10=sQuery(id+"F0.wireOp",EDGE,"E23.filletArc");var subQ11=sQuery(id+"F0.wireOp",EDGE,"E24.filletArc");Q0=makeQuery(id+"F2.boolean.opBoolean","SPLIT",FACE,{"disambiguationData":[TD([makeQuery(id+"F1.opExtrude","SWEPT_FACE",FACE,{"disambiguationData":[OSD([subQ6])]})])],"derivedFrom":makeQuery(id+"F1.opExtrude","CAP_FACE",FACE,{"disambiguationData":[OSD([subQ6,subQ8,subQ9,subQ7,subQ4,subQ3,subQ2,subQ1,subQ0,subQ5,subQ10,subQ11])],"isStart":true})});}
            var sketch = newSketch(context, id + "F16", { "sketchPlane" : qUnion([Q0])});
            skPoint(sketch, "E79.endSnap0", {"position": v(80, 0) * mm});
            skLineSegment(sketch, "E80", {"start": v(-22.42, 90) * mm, "end": v(-12.7, 108) * mm});
            skLineSegment(sketch, "E81", {"start": v(28.82, 90) * mm, "end": v(17.3, 108) * mm});
            skLineSegment(sketch, "E82", {"start": v(17.3, 108) * mm, "end": v(17.3, 119.96) * mm});
            skLineSegment(sketch, "E83", {"start": v(-12.7, 108) * mm, "end": v(-12.7, 120) * mm});
            skArc(sketch, "E84", {"start": v(17.3, 119.96) * mm, "mid": v(2.32, 135) * mm, "end": v(-12.7, 120) * mm});
            skPoint(sketch, "E85.endSnap0", {"position": v(62.93, 72.93) * mm});
            skLineSegment(sketch, "E86", {"start": v(2.3, 120) * mm, "end": v(2.3, 90) * mm, "construction": true});
            skCircle(sketch, "E87", {"center": v(2.3, 120) * mm, "radius": 7.5 * mm});
            skLineSegment(sketch, "E88", {"start": v(-128.94, 0) * mm, "end": v(150.43, 0) * mm, "construction": true});
            skPoint(sketch, "E88.endSnap0", {"position": v(60, 0) * mm});
            skLineSegment(sketch, "E89.MirrorCS", {"start": v(-12.7, -108) * mm, "end": v(-12.7, -120) * mm});
            skLineSegment(sketch, "E90.MirrorCS", {"start": v(17.3, -108) * mm, "end": v(17.3, -119.96) * mm});
            skLineSegment(sketch, "E91.MirrorCS", {"start": v(-22.42, -90) * mm, "end": v(-12.7, -108) * mm});
            skLineSegment(sketch, "E92.MirrorCS", {"start": v(28.82, -90) * mm, "end": v(17.3, -108) * mm});
            skCircle(sketch, "E93.MirrorC", {"center": v(2.3, -120) * mm, "radius": 7.5 * mm});
            skArc(sketch, "E94.MirrorCS", {"start": v(17.3, -119.96) * mm, "mid": v(2.32, -135) * mm, "end": v(-12.7, -120) * mm});
            skLineSegment(sketch, "E95.MirrorCS", {"start": v(2.3, -120) * mm, "end": v(2.3, -90) * mm, "construction": true});
            skSolve(sketch);
        }
        {
            var Q0;
            Q0=makeQuery(id+"F16.imprint","IMPRINT",FACE,{"disambiguationData":[TD([[makeQuery(id+"F16.imprint","IMPRINT",EDGE,{"derivedFrom":makeQuery(id+"F1.opExtrude","CAP_EDGE",EDGE,{"disambiguationData":[OSD([sQuery(id+"F0.wireOp",EDGE,"E1.left")])],"isStart":true})}),-1.0]])]});
            var Q1;
            Q1=makeQuery(id+"F16.imprint","IMPRINT",FACE,{"disambiguationData":[TD([[makeQuery(id+"F16.imprint","IMPRINT",EDGE,{"derivedFrom":sQuery(id+"F16.wireOp",EDGE,"0d30190f-5d67-49be-a1e4-9453548e4cf04.MirrorCS")}),1.0]])]});
            var Q2;
            {var subQ0=sQuery(id+"F16.wireOp",EDGE,"ufLeQcGq-YrwP-aZ7T-3zKd-vi4nBVnYJKsB");Q2=makeQuery(id+"F16.imprint","IMPRINT",FACE,{"disambiguationData":[TD([[makeQuery(id+"F16.imprint","IMPRINT",EDGE,{"derivedFrom":subQ0}),1.0]])]});}
            extrude(context, id + "F17", {"entities" : qUnion([Q0, Q1, Q2]), "operationType" : NewBodyOperationType.ADD, "depth" : 25 * mm});
        }
        {
            var Q0;
            Q0=makeQuery(id+"F16.imprint","IMPRINT",FACE,{"disambiguationData":[TD([[makeQuery(id+"F16.imprint","IMPRINT",EDGE,{"derivedFrom":makeQuery(id+"F1.opExtrude","CAP_EDGE",EDGE,{"disambiguationData":[OSD([sQuery(id+"F0.wireOp",EDGE,"E1.left")])],"isStart":true})}),-1.0]])]});
            var Q1;
            Q1=makeQuery(id+"F16.imprint","IMPRINT",FACE,{"disambiguationData":[TD([[makeQuery(id+"F16.imprint","IMPRINT",EDGE,{"derivedFrom":sQuery(id+"F16.wireOp",EDGE,"0d30190f-5d67-49be-a1e4-9453548e4cf00.MirrorCS")}),1.0]])]});
            var Q2;
            {var subQ2=sQuery(id+"F16.wireOp",EDGE,"A52O5LAY-q1ZF-Dxkz-vY2v-owyZFJAelKRb");Q2=makeQuery(id+"F16.imprint","IMPRINT",FACE,{"disambiguationData":[TD([[makeQuery(id+"F16.imprint","IMPRINT",EDGE,{"derivedFrom":subQ2}),-1.0]])]});}
            extrude(context, id + "F18", {"entities" : qUnion([Q0, Q1, Q2]), "operationType" : NewBodyOperationType.ADD, "depth" : 25 * mm});
        }
        {
            var Q0;
            Q0=makeQuery(id+"F16.imprint","IMPRINT",FACE,{"disambiguationData":[TD([[makeQuery(id+"F16.imprint","IMPRINT",EDGE,{"derivedFrom":makeQuery(id+"F1.opExtrude","CAP_EDGE",EDGE,{"disambiguationData":[OSD([sQuery(id+"F0.wireOp",EDGE,"E1.left")])],"isStart":true})}),-1.0]])]});
            var Q1;
            Q1=makeQuery(id+"F16.imprint","IMPRINT",FACE,{"disambiguationData":[TD([[makeQuery(id+"F16.imprint","IMPRINT",EDGE,{"derivedFrom":sQuery(id+"F16.wireOp",EDGE,"0d30190f-5d67-49be-a1e4-9453548e4cf00.MirrorCS")}),1.0]])]});
            var Q2;
            {var subQ2=sQuery(id+"F16.wireOp",EDGE,"A52O5LAY-q1ZF-Dxkz-vY2v-owyZFJAelKRb");Q2=makeQuery(id+"F16.imprint","IMPRINT",FACE,{"disambiguationData":[TD([[makeQuery(id+"F16.imprint","IMPRINT",EDGE,{"derivedFrom":subQ2}),-1.0]])]});}
            extrude(context, id + "F19", {"entities" : qUnion([Q0, Q1, Q2]), "operationType" : NewBodyOperationType.ADD, "depth" : 25 * mm});
        }
        {
            var Q0;
            Q0=makeQuery(id+"F16.imprint","IMPRINT",FACE,{"disambiguationData":[TD([[makeQuery(id+"F16.imprint","IMPRINT",EDGE,{"derivedFrom":makeQuery(id+"F1.opExtrude","CAP_EDGE",EDGE,{"disambiguationData":[OSD([sQuery(id+"F0.wireOp",EDGE,"E1.left")])],"isStart":true})}),-1.0]])]});
            var Q1;
            Q1=makeQuery(id+"F16.imprint","IMPRINT",FACE,{"disambiguationData":[TD([[makeQuery(id+"F16.imprint","IMPRINT",EDGE,{"derivedFrom":sQuery(id+"F16.wireOp",EDGE,"E89.MirrorCS")}),1.0]])]});
            var Q2;
            {var subQ0=sQuery(id+"F16.wireOp",EDGE,"E80");Q2=makeQuery(id+"F16.imprint","IMPRINT",FACE,{"disambiguationData":[TD([[makeQuery(id+"F16.imprint","IMPRINT",EDGE,{"derivedFrom":subQ0}),-1.0]])]});}
            extrude(context, id + "F20", {"entities" : qUnion([Q0, Q1, Q2]), "operationType" : NewBodyOperationType.ADD, "depth" : 25 * mm});
        }
    });
